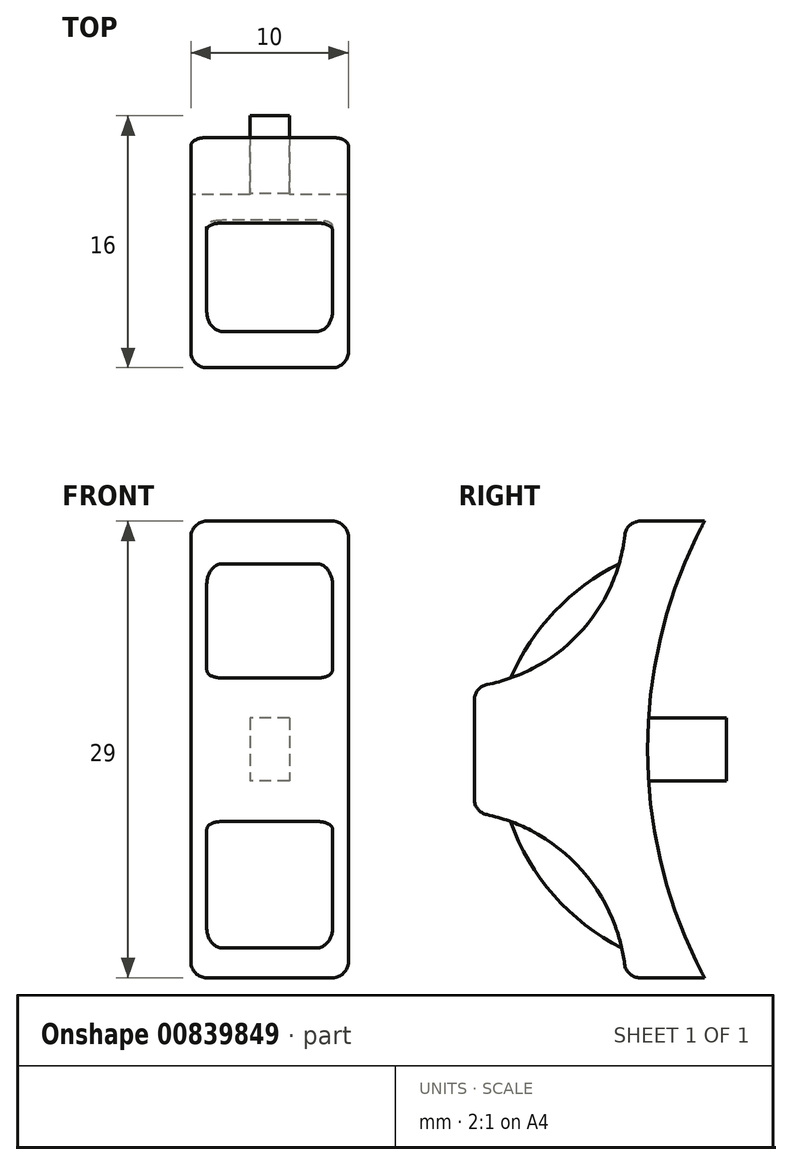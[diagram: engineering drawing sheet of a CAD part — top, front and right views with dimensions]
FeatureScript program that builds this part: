
annotation { "Feature Type Name" : "Feature", "Feature Type Description" : "" }
export const myFeature = defineFeature(function(context is Context, id is Id, definition is map)
    precondition{}
    {
        {
            var Q0;
            Q0=qCreatedBy(makeId("Right.planeOp"),FACE);
            var sketch = newSketch(context, id + "F0", { "sketchPlane" : qUnion([Q0])});
            skArc(sketch, "E0", {"start": v(0, -14.5) * mm, "mid": v(-3.62, 0) * mm, "end": v(0, 14.5) * mm});
            skLineSegment(sketch, "E1", {"start": v(0, 14.5) * mm, "end": v(-5, 14.5) * mm});
            skLineSegment(sketch, "E2", {"start": v(-14.62, 4) * mm, "end": v(-14.62, -4) * mm});
            skLineSegment(sketch, "E3", {"start": v(0, -14.5) * mm, "end": v(-5, -14.5) * mm});
            skLineSegment(sketch, "E4", {"start": v(-3.56, 2) * mm, "end": v(1.38, 2) * mm});
            skLineSegment(sketch, "E5", {"start": v(1.38, 2) * mm, "end": v(1.38, -2) * mm});
            skLineSegment(sketch, "E6", {"start": v(1.38, -2) * mm, "end": v(-3.56, -2) * mm});
            skArc(sketch, "E7", {"start": v(-14.62, 4) * mm, "mid": v(-7.86, 7.47) * mm, "end": v(-5, 14.5) * mm});
            skArc(sketch, "E8", {"start": v(-5, -14.5) * mm, "mid": v(-7.92, -7.52) * mm, "end": v(-14.62, -4) * mm});
            skArc(sketch, "E9", {"start": v(-5.43, 11.8) * mm, "mid": v(-9.51, 8.77) * mm, "end": v(-12.32, 4.53) * mm});
            skArc(sketch, "E10", {"start": v(-12.32, -4.57) * mm, "mid": v(-9.57, -9.27) * mm, "end": v(-5.26, -12.6) * mm});
            skSolve(sketch);
        }
        {
            var Q0;
            {var subQ6=sQuery(id+"F0.wireOp",EDGE,"E1");Q0=makeQuery(id+"F0.imprint","IMPRINT",FACE,{"disambiguationData":[TD([[makeQuery(id+"F0.imprint","IMPRINT",EDGE,{"derivedFrom":subQ6}),1.0]])]});}
            extrude(context, id + "F1", {"entities" : qUnion([Q0]), "endBound" : BoundingType.SYMMETRIC, "depth" : 10 * mm, "offsetDistance" : 25 * mm});
        }
        {
            var Q0;
            {var subQ0=sQuery(id+"F0.wireOp",EDGE,"E9");Q0=makeQuery(id+"F0.imprint","IMPRINT",FACE,{"disambiguationData":[TD([[makeQuery(id+"F0.imprint","IMPRINT",EDGE,{"derivedFrom":subQ0}),1.0]])]});}
            var Q1;
            {var subQ0=sQuery(id+"F0.wireOp",EDGE,"E10");Q1=makeQuery(id+"F0.imprint","IMPRINT",FACE,{"disambiguationData":[TD([[makeQuery(id+"F0.imprint","IMPRINT",EDGE,{"derivedFrom":subQ0}),1.0]])]});}
            extrude(context, id + "F2", {"entities" : qUnion([Q0, Q1]), "operationType" : NewBodyOperationType.ADD, "endBound" : BoundingType.SYMMETRIC, "depth" : 8 * mm, "offsetDistance" : 25 * mm});
        }
        {
            var Q0;
            {var subQ0=sQuery(id+"F0.wireOp",EDGE,"E4");Q0=makeQuery(id+"F0.imprint","IMPRINT",FACE,{"disambiguationData":[TD([[makeQuery(id+"F0.imprint","IMPRINT",EDGE,{"derivedFrom":subQ0}),-1.0]])]});}
            extrude(context, id + "F3", {"entities" : qUnion([Q0]), "operationType" : NewBodyOperationType.ADD, "endBound" : BoundingType.SYMMETRIC, "depth" : 2.5 * mm, "offsetDistance" : 25 * mm});
        }
        {
            var Q0;
            Q0=makeQuery(id+"F1.opExtrude","CAP_EDGE",EDGE,{"disambiguationData":[OSD([sQuery(id+"F0.wireOp",EDGE,"E2")])],"isStart":false});
            var Q1;
            Q1=makeQuery(id+"F1.opExtrude","CAP_EDGE",EDGE,{"disambiguationData":[OSD([sQuery(id+"F0.wireOp",EDGE,"E7")])],"isStart":false});
            var Q2;
            Q2=makeQuery(id+"F1.opExtrude","CAP_EDGE",EDGE,{"disambiguationData":[OSD([sQuery(id+"F0.wireOp",EDGE,"E8")])],"isStart":false});
            var Q3;
            Q3=makeQuery(id+"F1.opExtrude","CAP_EDGE",EDGE,{"disambiguationData":[OSD([sQuery(id+"F0.wireOp",EDGE,"E7")])],"isStart":true});
            var Q4;
            Q4=makeQuery(id+"F1.opExtrude","CAP_EDGE",EDGE,{"disambiguationData":[OSD([sQuery(id+"F0.wireOp",EDGE,"E2")])],"isStart":true});
            var Q5;
            Q5=makeQuery(id+"F1.opExtrude","CAP_EDGE",EDGE,{"disambiguationData":[OSD([sQuery(id+"F0.wireOp",EDGE,"E8")])],"isStart":true});
            var Q6;
            Q6=makeQuery(id+"F1.opExtrude","SWEPT_EDGE",EDGE,{"disambiguationData":[OSD([sQuery(id+"F0.wireOp",EDGE,"E1"),sQuery(id+"F0.wireOp",EDGE,"E7")])]});
            var Q7;
            Q7=makeQuery(id+"F1.opExtrude","SWEPT_EDGE",EDGE,{"disambiguationData":[OSD([sQuery(id+"F0.wireOp",EDGE,"E3"),sQuery(id+"F0.wireOp",EDGE,"E8")])]});
            var Q8;
            Q8=makeQuery(id+"F1.opExtrude","CAP_EDGE",EDGE,{"disambiguationData":[OSD([sQuery(id+"F0.wireOp",EDGE,"E1")])],"isStart":true});
            var Q9;
            Q9=makeQuery(id+"F1.opExtrude","CAP_EDGE",EDGE,{"disambiguationData":[OSD([sQuery(id+"F0.wireOp",EDGE,"E1")])],"isStart":false});
            var Q10;
            Q10=makeQuery(id+"F1.opExtrude","CAP_EDGE",EDGE,{"disambiguationData":[OSD([sQuery(id+"F0.wireOp",EDGE,"E3")])],"isStart":true});
            var Q11;
            Q11=makeQuery(id+"F1.opExtrude","CAP_EDGE",EDGE,{"disambiguationData":[OSD([sQuery(id+"F0.wireOp",EDGE,"E3")])],"isStart":false});
            var Q12;
            Q12=makeQuery(id+"F2.opExtrude","CAP_EDGE",EDGE,{"disambiguationData":[OSD([sQuery(id+"F0.wireOp",EDGE,"E10")])],"isStart":false});
            var Q13;
            Q13=makeQuery(id+"F2.opExtrude","CAP_EDGE",EDGE,{"disambiguationData":[OSD([sQuery(id+"F0.wireOp",EDGE,"E10")])],"isStart":true});
            var Q14;
            Q14=makeQuery(id+"F2.opExtrude","CAP_EDGE",EDGE,{"disambiguationData":[OSD([sQuery(id+"F0.wireOp",EDGE,"E9")])],"isStart":false});
            var Q15;
            Q15=makeQuery(id+"F2.opExtrude","CAP_EDGE",EDGE,{"disambiguationData":[OSD([sQuery(id+"F0.wireOp",EDGE,"E9")])],"isStart":true});
            var Q16;
            Q16=makeQuery(id+"F1.opExtrude","SWEPT_EDGE",EDGE,{"disambiguationData":[OSD([sQuery(id+"F0.wireOp",EDGE,"E2"),sQuery(id+"F0.wireOp",EDGE,"E7")])]});
            var Q17;
            Q17=makeQuery(id+"F1.opExtrude","SWEPT_EDGE",EDGE,{"disambiguationData":[OSD([sQuery(id+"F0.wireOp",EDGE,"E2"),sQuery(id+"F0.wireOp",EDGE,"E8")])]});
            fillet(context, id + "F4", {"entities" : qUnion([Q0, Q1, Q2, Q3, Q4, Q5, Q6, Q7, Q8, Q9, Q10, Q11, Q12, Q13, Q14, Q15, Q16, Q17]), "radius" : 1 * mm, "tangentPropagation" : true, "allowEdgeOverflow" : false});
        }
    });
